# Revit family: FB-185-19-1
name_source: partatom
category: Plumbing Fixtures
revit_build: Autodesk Revit 2014 (Build: 20130308_1515(x64)
units: mm (PartAtom-declared; Revit-internal decimal feet)

## types (1)
- FB-185-19-1
    CW Connection = Yes
    Certification = http://www.helvex.com.mx
    Chrome = Brass Chromed
    Compliance = NOM-005-CONAGUA-1996
    Connection = 1" Feeding Connection
    Description = 0.26" gpf, Battery Operated Electronic Urinal Flushvalve With Button
    Documentation = http://www.helvex.com.mx
    Features = Operates With a 6V Lithium Battery; Button With Antibacterial Coating; Left or Right Connection
    Feeding Voltage = 6 V
    Flow = 0.26 Gallons Per Flush
    Instructive = http://www.helvex.com.mx
    Manufacturer = Helvex
    Max. Working Pressure = 85.3 psi
    Min. Working Pressure = 14.2 psi
    Model = FB-185-19-1
    Note = Feeding Pipe Must Be 1 ¼" and Connection a 1 ¼" - 1" Reductor to Stop Valve
    Power Consumption = 2 W
    Type Comments = Flushvalves
    URL = http://www.helvex.com.mx

## geometry (parser evidence)
native form markers: Sweep x1
no freeform markers — native parametric forms only
